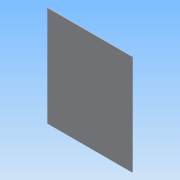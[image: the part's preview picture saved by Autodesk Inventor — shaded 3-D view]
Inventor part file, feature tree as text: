
AUTODESK INVENTOR PART (.ipt)
format: ipt  version: 2014 (Build 180170000, 170)  size: 82,944 bytes
history: native  units: in
note: dims shown in document units (in); Inventor stores cm internally (conversion verified against a paired STEP export)
features: reference x2, extrude x1, sketch x1
ambient origin geometry x8: Origin, YZ Plane, XZ Plane, XY Plane, X Axis, Y Axis, Z Axis, Center Point
bodies: Solid1 (feature_tree)
feature tree (4):
  extrude  "Extrusion1"  [1 undecoded]
  sketch  "Sketch1"  dims[d0=0.0625in d1=0.0in]
  reference  "Reference1"
  reference  "Reference2"
note: 1 required parameter value undecoded (feature->parameter linkage not recoverable at this tier; creation-order binding heuristic only, values carry confidence <= 0.55)
